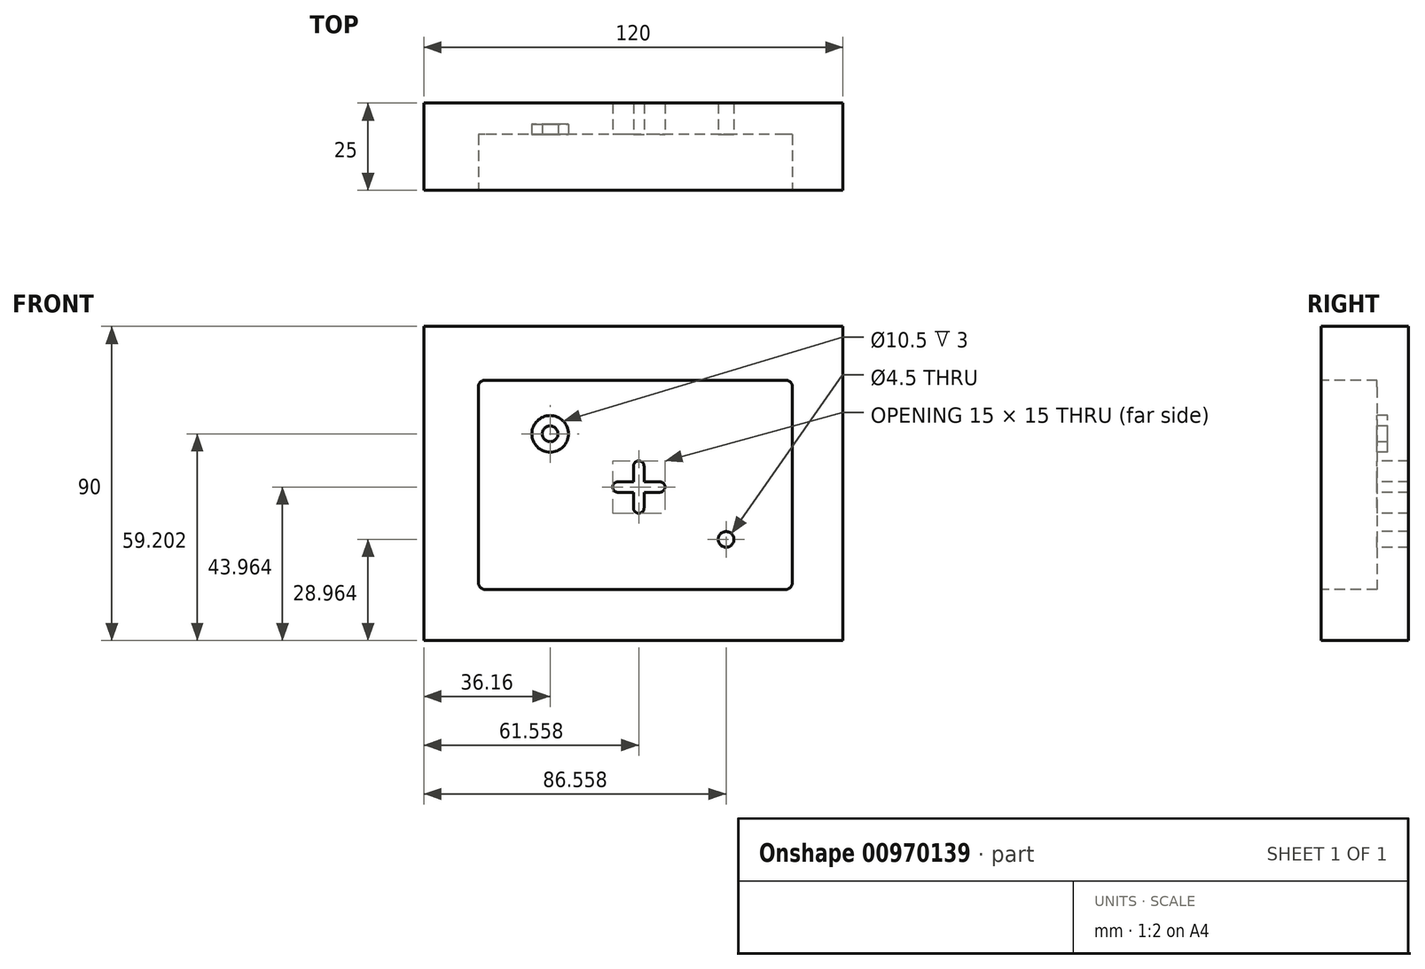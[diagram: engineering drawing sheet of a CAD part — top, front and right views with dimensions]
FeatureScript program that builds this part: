
annotation { "Feature Type Name" : "Feature", "Feature Type Description" : "" }
export const myFeature = defineFeature(function(context is Context, id is Id, definition is map)
    precondition{}
    {
        {
            var Q0;
            Q0=qCreatedBy(makeId("Front.planeOp"),FACE);
            var sketch = newSketch(context, id + "F0", { "sketchPlane" : qUnion([Q0])});
            skLineSegment(sketch, "E0.bottom", {"start": v(60, 45) * mm, "end": v(-60, 45) * mm});
            skLineSegment(sketch, "E0.top", {"start": v(60, -45) * mm, "end": v(-60, -45) * mm});
            skLineSegment(sketch, "E0.left", {"start": v(60, 45) * mm, "end": v(60, -45) * mm});
            skLineSegment(sketch, "E0.right", {"start": v(-60, 45) * mm, "end": v(-60, -45) * mm});
            skPoint(sketch, "E0.middle", {"position": v(0, 0) * mm});
            skLineSegment(sketch, "E1.bottom", {"start": v(43, 30) * mm, "end": v(-43, 30) * mm});
            skLineSegment(sketch, "E1.top", {"start": v(43, -30) * mm, "end": v(-43, -30) * mm});
            skLineSegment(sketch, "E1.left", {"start": v(45, 28) * mm, "end": v(45, -28) * mm});
            skLineSegment(sketch, "E1.right", {"start": v(-45, 28) * mm, "end": v(-45, -28) * mm});
            skPoint(sketch, "E2.visualSharp", {"position": v(-45, 30) * mm});
            skArc(sketch, "E2.filletArc", {"start": v(-43, 30) * mm, "mid": v(-44.41, 29.41) * mm, "end": v(-45, 28) * mm});
            skPoint(sketch, "E3.visualSharp", {"position": v(45, 30) * mm});
            skArc(sketch, "E3.filletArc", {"start": v(45, 28) * mm, "mid": v(44.41, 29.41) * mm, "end": v(43, 30) * mm});
            skPoint(sketch, "E4.visualSharp", {"position": v(45, -30) * mm});
            skArc(sketch, "E4.filletArc", {"start": v(43, -30) * mm, "mid": v(44.41, -29.41) * mm, "end": v(45, -28) * mm});
            skPoint(sketch, "E5.visualSharp", {"position": v(-45, -30) * mm});
            skArc(sketch, "E5.filletArc", {"start": v(-45, -28) * mm, "mid": v(-44.41, -29.41) * mm, "end": v(-43, -30) * mm});
            skCircle(sketch, "E6", {"center": v(-25, 15) * mm, "radius": 2.25 * mm});
            skCircle(sketch, "E7", {"center": v(-25, 15) * mm, "radius": 5.25 * mm});
            skCircle(sketch, "E8", {"center": v(25, -15) * mm, "radius": 2.25 * mm});
            skLineSegment(sketch, "E9.bottom", {"start": v(6, 1.5) * mm, "end": v(1.5, 1.5) * mm});
            skLineSegment(sketch, "E9.top", {"start": v(6, -1.5) * mm, "end": v(1.5, -1.5) * mm});
            skLineSegment(sketch, "E9.left", {"start": v(7.5, 0) * mm, "end": v(7.5, 0) * mm});
            skLineSegment(sketch, "E9.right", {"start": v(-7.5, 0) * mm, "end": v(-7.5, 0) * mm});
            skPoint(sketch, "E10.visualSharp", {"position": v(7.5, 1.5) * mm});
            skArc(sketch, "E10.filletArc", {"start": v(7.5, 0) * mm, "mid": v(7.06, 1.06) * mm, "end": v(6, 1.5) * mm});
            skPoint(sketch, "E11.visualSharp", {"position": v(7.5, -1.5) * mm});
            skArc(sketch, "E11.filletArc", {"start": v(6, -1.5) * mm, "mid": v(7.06, -1.06) * mm, "end": v(7.5, 0) * mm});
            skPoint(sketch, "E12.visualSharp", {"position": v(-7.5, -1.5) * mm});
            skArc(sketch, "E12.filletArc", {"start": v(-7.5, 0) * mm, "mid": v(-7.06, -1.06) * mm, "end": v(-6, -1.5) * mm});
            skPoint(sketch, "E13.visualSharp", {"position": v(-7.5, 1.5) * mm});
            skArc(sketch, "E13.filletArc", {"start": v(-6, 1.5) * mm, "mid": v(-7.06, 1.06) * mm, "end": v(-7.5, 0) * mm});
            skLineSegment(sketch, "E14.1.0", {"start": v(1.5, -6) * mm, "end": v(1.5, -1.5) * mm});
            skArc(sketch, "E14.1.1", {"start": v(1.5, 6) * mm, "mid": v(1.06, 7.06) * mm, "end": v(0, 7.5) * mm});
            skArc(sketch, "E14.1.2", {"start": v(0, 7.5) * mm, "mid": v(-1.06, 7.06) * mm, "end": v(-1.5, 6) * mm});
            skLineSegment(sketch, "E14.1.3", {"start": v(-1.5, -6) * mm, "end": v(-1.5, -1.5) * mm});
            skArc(sketch, "E14.1.4", {"start": v(-1.5, -6) * mm, "mid": v(-1.06, -7.06) * mm, "end": v(0, -7.5) * mm});
            skArc(sketch, "E14.1.5", {"start": v(0, -7.5) * mm, "mid": v(1.06, -7.06) * mm, "end": v(1.5, -6) * mm});
            skLineSegment(sketch, "E14.anchor1", {"start": v(0, 0) * mm, "end": v(-6, 1.5) * mm, "construction": true});
            skLineSegment(sketch, "E14.anchor2", {"start": v(0, 0) * mm, "end": v(1.5, 6) * mm, "construction": true});
            skLineSegment(sketch, "E15.trimOffspring", {"start": v(-1.5, 1.5) * mm, "end": v(-6, 1.5) * mm});
            skLineSegment(sketch, "E16.trimOffspring", {"start": v(-1.5, 1.5) * mm, "end": v(-1.5, 6) * mm});
            skLineSegment(sketch, "E17.trimOffspring", {"start": v(1.5, 1.5) * mm, "end": v(1.5, 6) * mm});
            skLineSegment(sketch, "E18.trimOffspring", {"start": v(-1.5, -1.5) * mm, "end": v(-6, -1.5) * mm});
            skSolve(sketch);
        }
        {
            var Q0;
            Q0=makeQuery(id+"F0.imprint","IMPRINT",FACE,{"disambiguationData":[TD([[makeQuery(id+"F0.imprint","IMPRINT",EDGE,{"derivedFrom":sQuery(id+"F0.wireOp",EDGE,"E1.bottom")}),1.0]])]});
            var Q1;
            Q1=makeQuery(id+"F0.imprint","IMPRINT",FACE,{"disambiguationData":[TD([[makeQuery(id+"F0.imprint","IMPRINT",EDGE,{"derivedFrom":sQuery(id+"F0.wireOp",EDGE,"E0.bottom")}),1.0]])]});
            var Q2;
            Q2=makeQuery(id+"F0.imprint","IMPRINT",FACE,{"disambiguationData":[TD([[makeQuery(id+"F0.imprint","IMPRINT",EDGE,{"derivedFrom":sQuery(id+"F0.wireOp",EDGE,"E6")}),1.0]])]});
            var Q3;
            Q3=makeQuery(id+"F0.imprint","IMPRINT",FACE,{"disambiguationData":[TD([[makeQuery(id+"F0.imprint","IMPRINT",EDGE,{"derivedFrom":sQuery(id+"F0.wireOp",EDGE,"E6")}),-1.0]])]});
            var Q4;
            Q4=makeQuery(id+"F0.imprint","IMPRINT",FACE,{"disambiguationData":[TD([[makeQuery(id+"F0.imprint","IMPRINT",EDGE,{"derivedFrom":sQuery(id+"F0.wireOp",EDGE,"E9.bottom")}),1.0]])]});
            var Q5;
            Q5=makeQuery(id+"F0.imprint","IMPRINT",FACE,{"disambiguationData":[TD([[makeQuery(id+"F0.imprint","IMPRINT",EDGE,{"derivedFrom":sQuery(id+"F0.wireOp",EDGE,"E8")}),1.0]])]});
            extrude(context, id + "F1", {"entities" : qUnion([Q0, Q1, Q2, Q3, Q4, Q5]), "oppositeDirection" : true, "depth" : 25 * mm, "offsetDistance" : 25 * mm});
        }
        {
            var Q0;
            Q0=makeQuery(id+"F1.opExtrude","CAP_FACE",FACE,{"disambiguationData":[OSD([sQuery(id+"F0.wireOp",EDGE,"E0.bottom"),sQuery(id+"F0.wireOp",EDGE,"E0.top"),sQuery(id+"F0.wireOp",EDGE,"E0.left"),sQuery(id+"F0.wireOp",EDGE,"E0.right")])],"isStart":true});
            var sketch = newSketch(context, id + "F2", { "sketchPlane" : qUnion([Q0])});
            skLineSegment(sketch, "E19.bottom", {"start": v(60.58, 44.6) * mm, "end": v(-59.42, 44.6) * mm});
            skLineSegment(sketch, "E19.top", {"start": v(60.58, -45.4) * mm, "end": v(-59.42, -45.4) * mm});
            skLineSegment(sketch, "E19.left", {"start": v(60.58, 44.6) * mm, "end": v(60.58, -45.4) * mm});
            skLineSegment(sketch, "E19.right", {"start": v(-59.42, 44.6) * mm, "end": v(-59.42, -45.4) * mm});
            skPoint(sketch, "E19.middle", {"position": v(0.58, -0.4) * mm});
            skLineSegment(sketch, "E20.bottom", {"start": v(43.58, 29.6) * mm, "end": v(-42.42, 29.6) * mm});
            skLineSegment(sketch, "E20.top", {"start": v(43.58, -30.4) * mm, "end": v(-42.42, -30.4) * mm});
            skLineSegment(sketch, "E20.left", {"start": v(45.58, 27.6) * mm, "end": v(45.58, -28.4) * mm});
            skLineSegment(sketch, "E20.right", {"start": v(-44.42, 27.6) * mm, "end": v(-44.42, -28.4) * mm});
            skPoint(sketch, "E21.visualSharp", {"position": v(-44.42, 29.6) * mm});
            skArc(sketch, "E21.filletArc", {"start": v(-42.42, 29.6) * mm, "mid": v(-43.83, 29.02) * mm, "end": v(-44.42, 27.6) * mm});
            skPoint(sketch, "E22.visualSharp", {"position": v(45.58, 29.6) * mm});
            skArc(sketch, "E22.filletArc", {"start": v(45.58, 27.6) * mm, "mid": v(45, 29.02) * mm, "end": v(43.58, 29.6) * mm});
            skPoint(sketch, "E23.visualSharp", {"position": v(45.58, -30.4) * mm});
            skArc(sketch, "E23.filletArc", {"start": v(43.58, -30.4) * mm, "mid": v(45, -29.81) * mm, "end": v(45.58, -28.4) * mm});
            skPoint(sketch, "E24.visualSharp", {"position": v(-44.42, -30.4) * mm});
            skArc(sketch, "E24.filletArc", {"start": v(-44.42, -28.4) * mm, "mid": v(-43.83, -29.81) * mm, "end": v(-42.42, -30.4) * mm});
            skCircle(sketch, "E25", {"center": v(-24.42, 14.6) * mm, "radius": 2.25 * mm});
            skCircle(sketch, "E26", {"center": v(-24.42, 14.6) * mm, "radius": 5.25 * mm});
            skCircle(sketch, "E27", {"center": v(25.58, -15.4) * mm, "radius": 2.25 * mm});
            skLineSegment(sketch, "E28.bottom", {"start": v(6.58, 1.1) * mm, "end": v(2.08, 1.1) * mm});
            skLineSegment(sketch, "E28.top", {"start": v(6.58, -1.9) * mm, "end": v(2.08, -1.9) * mm});
            skLineSegment(sketch, "E28.left", {"start": v(8.08, -0.4) * mm, "end": v(8.08, -0.4) * mm});
            skLineSegment(sketch, "E28.right", {"start": v(-6.92, -0.4) * mm, "end": v(-6.92, -0.4) * mm});
            skPoint(sketch, "E29.visualSharp", {"position": v(8.08, 1.1) * mm});
            skArc(sketch, "E29.filletArc", {"start": v(8.08, -0.4) * mm, "mid": v(7.64, 0.66) * mm, "end": v(6.58, 1.1) * mm});
            skPoint(sketch, "E30.visualSharp", {"position": v(8.08, -1.9) * mm});
            skArc(sketch, "E30.filletArc", {"start": v(6.58, -1.9) * mm, "mid": v(7.64, -1.46) * mm, "end": v(8.08, -0.4) * mm});
            skPoint(sketch, "E31.visualSharp", {"position": v(-6.92, -1.9) * mm});
            skArc(sketch, "E31.filletArc", {"start": v(-6.92, -0.4) * mm, "mid": v(-6.48, -1.46) * mm, "end": v(-5.42, -1.9) * mm});
            skPoint(sketch, "E32.visualSharp", {"position": v(-6.92, 1.1) * mm});
            skArc(sketch, "E32.filletArc", {"start": v(-5.42, 1.1) * mm, "mid": v(-6.48, 0.66) * mm, "end": v(-6.92, -0.4) * mm});
            skLineSegment(sketch, "E33.1.0", {"start": v(2.08, -6.4) * mm, "end": v(2.08, -1.9) * mm});
            skArc(sketch, "E33.1.1", {"start": v(2.08, 5.6) * mm, "mid": v(1.64, 6.66) * mm, "end": v(0.58, 7.1) * mm});
            skArc(sketch, "E33.1.2", {"start": v(0.58, 7.1) * mm, "mid": v(-0.48, 6.66) * mm, "end": v(-0.92, 5.6) * mm});
            skLineSegment(sketch, "E33.1.3", {"start": v(-0.92, -6.4) * mm, "end": v(-0.92, -1.9) * mm});
            skArc(sketch, "E33.1.4", {"start": v(-0.92, -6.4) * mm, "mid": v(-0.48, -7.46) * mm, "end": v(0.58, -7.9) * mm});
            skArc(sketch, "E33.1.5", {"start": v(0.58, -7.9) * mm, "mid": v(1.64, -7.46) * mm, "end": v(2.08, -6.4) * mm});
            skLineSegment(sketch, "E33.anchor1", {"start": v(0.58, -0.4) * mm, "end": v(-5.42, 1.1) * mm, "construction": true});
            skLineSegment(sketch, "E33.anchor2", {"start": v(0.58, -0.4) * mm, "end": v(2.08, 5.6) * mm, "construction": true});
            skLineSegment(sketch, "E34.trimOffspring", {"start": v(-0.92, 1.1) * mm, "end": v(-5.42, 1.1) * mm});
            skLineSegment(sketch, "E35.trimOffspring", {"start": v(-0.92, 1.1) * mm, "end": v(-0.92, 5.6) * mm});
            skLineSegment(sketch, "E36.trimOffspring", {"start": v(2.08, 1.1) * mm, "end": v(2.08, 5.6) * mm});
            skLineSegment(sketch, "E37.trimOffspring", {"start": v(-0.92, -1.9) * mm, "end": v(-5.42, -1.9) * mm});
            skSolve(sketch);
        }
        {
            var Q0;
            Q0=makeQuery(id+"F2.imprint","IMPRINT",FACE,{"disambiguationData":[TD([[makeQuery(id+"F2.imprint","IMPRINT",EDGE,{"derivedFrom":sQuery(id+"F2.wireOp",EDGE,"E20.bottom")}),1.0]])]});
            var Q1;
            Q1=makeQuery(id+"F2.imprint","IMPRINT",FACE,{"disambiguationData":[TD([[makeQuery(id+"F2.imprint","IMPRINT",EDGE,{"derivedFrom":sQuery(id+"F2.wireOp",EDGE,"E25")}),-1.0]])]});
            var Q2;
            Q2=makeQuery(id+"F2.imprint","IMPRINT",FACE,{"disambiguationData":[TD([[makeQuery(id+"F2.imprint","IMPRINT",EDGE,{"derivedFrom":sQuery(id+"F2.wireOp",EDGE,"E25")}),1.0]])]});
            var Q3;
            Q3=makeQuery(id+"F2.imprint","IMPRINT",FACE,{"disambiguationData":[TD([[makeQuery(id+"F2.imprint","IMPRINT",EDGE,{"derivedFrom":sQuery(id+"F2.wireOp",EDGE,"E28.bottom")}),1.0]])]});
            var Q4;
            Q4=makeQuery(id+"F2.imprint","IMPRINT",FACE,{"disambiguationData":[TD([[makeQuery(id+"F2.imprint","IMPRINT",EDGE,{"derivedFrom":sQuery(id+"F2.wireOp",EDGE,"E27")}),1.0]])]});
            extrude(context, id + "F3", {"entities" : qUnion([Q0, Q1, Q2, Q3, Q4]), "operationType" : NewBodyOperationType.REMOVE, "oppositeDirection" : true, "depth" : 16 * mm, "offsetDistance" : 25 * mm});
        }
        {
            var Q0;
            Q0=makeQuery(id+"F3.boolean.opBoolean","COPY",FACE,{"derivedFrom":makeQuery(id+"F3.opExtrude","CAP_FACE",FACE,{"disambiguationData":[OSD([sQuery(id+"F2.wireOp",EDGE,"E20.bottom"),sQuery(id+"F2.wireOp",EDGE,"E20.top"),sQuery(id+"F2.wireOp",EDGE,"E20.left"),sQuery(id+"F2.wireOp",EDGE,"E20.right"),sQuery(id+"F2.wireOp",EDGE,"E21.filletArc"),sQuery(id+"F2.wireOp",EDGE,"E22.filletArc"),sQuery(id+"F2.wireOp",EDGE,"E23.filletArc"),sQuery(id+"F2.wireOp",EDGE,"E24.filletArc")])],"isStart":false})});
            var sketch = newSketch(context, id + "F4", { "sketchPlane" : qUnion([Q0])});
            skLineSegment(sketch, "E38.bottom", {"start": v(61.16, 44.2) * mm, "end": v(-58.84, 44.2) * mm});
            skLineSegment(sketch, "E38.top", {"start": v(61.16, -45.8) * mm, "end": v(-58.84, -45.8) * mm});
            skLineSegment(sketch, "E38.left", {"start": v(61.16, 44.2) * mm, "end": v(61.16, -45.8) * mm});
            skLineSegment(sketch, "E38.right", {"start": v(-58.84, 44.2) * mm, "end": v(-58.84, -45.8) * mm});
            skPoint(sketch, "E38.middle", {"position": v(1.16, -0.8) * mm});
            skLineSegment(sketch, "E39.bottom", {"start": v(44.16, 29.2) * mm, "end": v(-41.84, 29.2) * mm});
            skLineSegment(sketch, "E39.top", {"start": v(44.16, -30.8) * mm, "end": v(-41.84, -30.8) * mm});
            skLineSegment(sketch, "E39.left", {"start": v(46.16, 27.2) * mm, "end": v(46.16, -28.8) * mm});
            skLineSegment(sketch, "E39.right", {"start": v(-43.84, 27.2) * mm, "end": v(-43.84, -28.8) * mm});
            skPoint(sketch, "E40.visualSharp", {"position": v(-43.84, 29.2) * mm});
            skArc(sketch, "E40.filletArc", {"start": v(-41.84, 29.2) * mm, "mid": v(-43.25, 28.62) * mm, "end": v(-43.84, 27.2) * mm});
            skPoint(sketch, "E41.visualSharp", {"position": v(46.16, 29.2) * mm});
            skArc(sketch, "E41.filletArc", {"start": v(46.16, 27.2) * mm, "mid": v(45.57, 28.62) * mm, "end": v(44.16, 29.2) * mm});
            skPoint(sketch, "E42.visualSharp", {"position": v(46.16, -30.8) * mm});
            skArc(sketch, "E42.filletArc", {"start": v(44.16, -30.8) * mm, "mid": v(45.57, -30.21) * mm, "end": v(46.16, -28.8) * mm});
            skPoint(sketch, "E43.visualSharp", {"position": v(-43.84, -30.8) * mm});
            skArc(sketch, "E43.filletArc", {"start": v(-43.84, -28.8) * mm, "mid": v(-43.25, -30.21) * mm, "end": v(-41.84, -30.8) * mm});
            skCircle(sketch, "E44", {"center": v(-23.84, 14.2) * mm, "radius": 2.25 * mm});
            skCircle(sketch, "E45", {"center": v(-23.84, 14.2) * mm, "radius": 5.25 * mm});
            skCircle(sketch, "E46", {"center": v(26.16, -15.8) * mm, "radius": 2.25 * mm});
            skLineSegment(sketch, "E47.bottom", {"start": v(7.16, 0.7) * mm, "end": v(2.66, 0.7) * mm});
            skLineSegment(sketch, "E47.top", {"start": v(7.16, -2.3) * mm, "end": v(2.66, -2.3) * mm});
            skLineSegment(sketch, "E47.left", {"start": v(8.66, -0.8) * mm, "end": v(8.66, -0.8) * mm});
            skLineSegment(sketch, "E47.right", {"start": v(-6.34, -0.8) * mm, "end": v(-6.34, -0.8) * mm});
            skPoint(sketch, "E48.visualSharp", {"position": v(8.66, 0.7) * mm});
            skArc(sketch, "E48.filletArc", {"start": v(8.66, -0.8) * mm, "mid": v(8.22, 0.26) * mm, "end": v(7.16, 0.7) * mm});
            skPoint(sketch, "E49.visualSharp", {"position": v(8.66, -2.3) * mm});
            skArc(sketch, "E49.filletArc", {"start": v(7.16, -2.3) * mm, "mid": v(8.22, -1.86) * mm, "end": v(8.66, -0.8) * mm});
            skPoint(sketch, "E50.visualSharp", {"position": v(-6.34, -2.3) * mm});
            skArc(sketch, "E50.filletArc", {"start": v(-6.34, -0.8) * mm, "mid": v(-5.9, -1.86) * mm, "end": v(-4.84, -2.3) * mm});
            skPoint(sketch, "E51.visualSharp", {"position": v(-6.34, 0.7) * mm});
            skArc(sketch, "E51.filletArc", {"start": v(-4.84, 0.7) * mm, "mid": v(-5.9, 0.26) * mm, "end": v(-6.34, -0.8) * mm});
            skLineSegment(sketch, "E52.1.0", {"start": v(2.66, -6.8) * mm, "end": v(2.66, -2.3) * mm});
            skArc(sketch, "E52.1.1", {"start": v(2.66, 5.2) * mm, "mid": v(2.22, 6.26) * mm, "end": v(1.16, 6.7) * mm});
            skArc(sketch, "E52.1.2", {"start": v(1.16, 6.7) * mm, "mid": v(0.1, 6.26) * mm, "end": v(-0.34, 5.2) * mm});
            skLineSegment(sketch, "E52.1.3", {"start": v(-0.34, -6.8) * mm, "end": v(-0.34, -2.3) * mm});
            skArc(sketch, "E52.1.4", {"start": v(-0.34, -6.8) * mm, "mid": v(0.1, -7.86) * mm, "end": v(1.16, -8.3) * mm});
            skArc(sketch, "E52.1.5", {"start": v(1.16, -8.3) * mm, "mid": v(2.22, -7.86) * mm, "end": v(2.66, -6.8) * mm});
            skLineSegment(sketch, "E52.anchor1", {"start": v(1.16, -0.8) * mm, "end": v(-4.84, 0.7) * mm, "construction": true});
            skLineSegment(sketch, "E52.anchor2", {"start": v(1.16, -0.8) * mm, "end": v(2.66, 5.2) * mm, "construction": true});
            skLineSegment(sketch, "E53.trimOffspring", {"start": v(-0.34, 0.7) * mm, "end": v(-4.84, 0.7) * mm});
            skLineSegment(sketch, "E54.trimOffspring", {"start": v(-0.34, 0.7) * mm, "end": v(-0.34, 5.2) * mm});
            skLineSegment(sketch, "E55.trimOffspring", {"start": v(2.66, 0.7) * mm, "end": v(2.66, 5.2) * mm});
            skLineSegment(sketch, "E56.trimOffspring", {"start": v(-0.34, -2.3) * mm, "end": v(-4.84, -2.3) * mm});
            skSolve(sketch);
        }
        {
            var Q0;
            Q0=makeQuery(id+"F4.imprint","IMPRINT",FACE,{"disambiguationData":[TD([[makeQuery(id+"F4.imprint","IMPRINT",EDGE,{"derivedFrom":sQuery(id+"F4.wireOp",EDGE,"E44")}),-1.0]])]});
            extrude(context, id + "F5", {"entities" : qUnion([Q0]), "operationType" : NewBodyOperationType.REMOVE, "oppositeDirection" : true, "depth" : 3 * mm, "offsetDistance" : 25 * mm});
        }
        {
            var Q0;
            {var subQ0=sQuery(id+"F2.wireOp",EDGE,"E20.right");var subQ1=sQuery(id+"F2.wireOp",EDGE,"E20.left");var subQ2=sQuery(id+"F2.wireOp",EDGE,"E20.top");var subQ3=sQuery(id+"F2.wireOp",EDGE,"E20.bottom");var subQ4=sQuery(id+"F2.wireOp",EDGE,"E21.filletArc");var subQ5=sQuery(id+"F2.wireOp",EDGE,"E22.filletArc");var subQ6=sQuery(id+"F2.wireOp",EDGE,"E23.filletArc");var subQ7=sQuery(id+"F2.wireOp",EDGE,"E24.filletArc");Q0=makeQuery(id+"F5.boolean.opBoolean","SPLIT",FACE,{"disambiguationData":[TD([makeQuery(id+"F3.boolean.opBoolean","COPY",FACE,{"derivedFrom":makeQuery(id+"F3.opExtrude","SWEPT_FACE",FACE,{"disambiguationData":[OSD([subQ3])]})})])],"derivedFrom":makeQuery(id+"F3.boolean.opBoolean","COPY",FACE,{"derivedFrom":makeQuery(id+"F3.opExtrude","CAP_FACE",FACE,{"disambiguationData":[OSD([subQ3,subQ2,subQ1,subQ0,subQ4,subQ5,subQ6,subQ7])],"isStart":false})})});}
            var sketch = newSketch(context, id + "F6", { "sketchPlane" : qUnion([Q0])});
            skLineSegment(sketch, "E57.bottom", {"start": v(61.56, 43.96) * mm, "end": v(-58.44, 43.96) * mm});
            skLineSegment(sketch, "E57.top", {"start": v(61.56, -46.04) * mm, "end": v(-58.44, -46.04) * mm});
            skLineSegment(sketch, "E57.left", {"start": v(61.56, 43.96) * mm, "end": v(61.56, -46.04) * mm});
            skLineSegment(sketch, "E57.right", {"start": v(-58.44, 43.96) * mm, "end": v(-58.44, -46.04) * mm});
            skPoint(sketch, "E57.middle", {"position": v(1.56, -1.04) * mm});
            skLineSegment(sketch, "E58.bottom", {"start": v(44.56, 28.96) * mm, "end": v(-41.44, 28.96) * mm});
            skLineSegment(sketch, "E58.top", {"start": v(44.56, -31.04) * mm, "end": v(-41.44, -31.04) * mm});
            skLineSegment(sketch, "E58.left", {"start": v(46.56, 26.96) * mm, "end": v(46.56, -29.04) * mm});
            skLineSegment(sketch, "E58.right", {"start": v(-43.44, 26.96) * mm, "end": v(-43.44, -29.04) * mm});
            skPoint(sketch, "E59.visualSharp", {"position": v(-43.44, 28.96) * mm});
            skArc(sketch, "E59.filletArc", {"start": v(-41.44, 28.96) * mm, "mid": v(-42.86, 28.38) * mm, "end": v(-43.44, 26.96) * mm});
            skPoint(sketch, "E60.visualSharp", {"position": v(46.56, 28.96) * mm});
            skArc(sketch, "E60.filletArc", {"start": v(46.56, 26.96) * mm, "mid": v(45.97, 28.38) * mm, "end": v(44.56, 28.96) * mm});
            skPoint(sketch, "E61.visualSharp", {"position": v(46.56, -31.04) * mm});
            skArc(sketch, "E61.filletArc", {"start": v(44.56, -31.04) * mm, "mid": v(45.97, -30.45) * mm, "end": v(46.56, -29.04) * mm});
            skPoint(sketch, "E62.visualSharp", {"position": v(-43.44, -31.04) * mm});
            skArc(sketch, "E62.filletArc", {"start": v(-43.44, -29.04) * mm, "mid": v(-42.86, -30.45) * mm, "end": v(-41.44, -31.04) * mm});
            skCircle(sketch, "E63", {"center": v(-23.44, 13.96) * mm, "radius": 2.25 * mm});
            skCircle(sketch, "E64", {"center": v(-23.44, 13.96) * mm, "radius": 5.25 * mm});
            skCircle(sketch, "E65", {"center": v(26.56, -16.04) * mm, "radius": 2.25 * mm});
            skLineSegment(sketch, "E66.bottom", {"start": v(7.56, 0.46) * mm, "end": v(3.06, 0.46) * mm});
            skLineSegment(sketch, "E66.top", {"start": v(7.56, -2.54) * mm, "end": v(3.06, -2.54) * mm});
            skLineSegment(sketch, "E66.left", {"start": v(9.06, -1.04) * mm, "end": v(9.06, -1.04) * mm});
            skLineSegment(sketch, "E66.right", {"start": v(-5.94, -1.04) * mm, "end": v(-5.94, -1.04) * mm});
            skPoint(sketch, "E67.visualSharp", {"position": v(9.06, 0.46) * mm});
            skArc(sketch, "E67.filletArc", {"start": v(9.06, -1.04) * mm, "mid": v(8.62, 0.02) * mm, "end": v(7.56, 0.46) * mm});
            skPoint(sketch, "E68.visualSharp", {"position": v(9.06, -2.54) * mm});
            skArc(sketch, "E68.filletArc", {"start": v(7.56, -2.54) * mm, "mid": v(8.62, -2.1) * mm, "end": v(9.06, -1.04) * mm});
            skPoint(sketch, "E69.visualSharp", {"position": v(-5.94, -2.54) * mm});
            skArc(sketch, "E69.filletArc", {"start": v(-5.94, -1.04) * mm, "mid": v(-5.5, -2.1) * mm, "end": v(-4.44, -2.54) * mm});
            skPoint(sketch, "E70.visualSharp", {"position": v(-5.94, 0.46) * mm});
            skArc(sketch, "E70.filletArc", {"start": v(-4.44, 0.46) * mm, "mid": v(-5.5, 0.02) * mm, "end": v(-5.94, -1.04) * mm});
            skLineSegment(sketch, "E71.1.0", {"start": v(3.06, -7.04) * mm, "end": v(3.06, -2.54) * mm});
            skArc(sketch, "E71.1.1", {"start": v(3.06, 4.96) * mm, "mid": v(2.62, 6.02) * mm, "end": v(1.56, 6.46) * mm});
            skArc(sketch, "E71.1.2", {"start": v(1.56, 6.46) * mm, "mid": v(0.5, 6.02) * mm, "end": v(0.06, 4.96) * mm});
            skLineSegment(sketch, "E71.1.3", {"start": v(0.06, -7.04) * mm, "end": v(0.06, -2.54) * mm});
            skArc(sketch, "E71.1.4", {"start": v(0.06, -7.04) * mm, "mid": v(0.5, -8.1) * mm, "end": v(1.56, -8.54) * mm});
            skArc(sketch, "E71.1.5", {"start": v(1.56, -8.54) * mm, "mid": v(2.62, -8.1) * mm, "end": v(3.06, -7.04) * mm});
            skLineSegment(sketch, "E71.anchor1", {"start": v(1.56, -1.04) * mm, "end": v(-4.44, 0.46) * mm, "construction": true});
            skLineSegment(sketch, "E71.anchor2", {"start": v(1.56, -1.04) * mm, "end": v(3.06, 4.96) * mm, "construction": true});
            skLineSegment(sketch, "E72.trimOffspring", {"start": v(0.06, 0.46) * mm, "end": v(-4.44, 0.46) * mm});
            skLineSegment(sketch, "E73.trimOffspring", {"start": v(0.06, 0.46) * mm, "end": v(0.06, 4.96) * mm});
            skLineSegment(sketch, "E74.trimOffspring", {"start": v(3.06, 0.46) * mm, "end": v(3.06, 4.96) * mm});
            skLineSegment(sketch, "E75.trimOffspring", {"start": v(0.06, -2.54) * mm, "end": v(-4.44, -2.54) * mm});
            skSolve(sketch);
        }
        {
            var Q0;
            Q0=makeQuery(id+"F6.imprint","IMPRINT",FACE,{"disambiguationData":[TD([[makeQuery(id+"F6.imprint","IMPRINT",EDGE,{"derivedFrom":sQuery(id+"F6.wireOp",EDGE,"E66.bottom")}),1.0]])]});
            var Q1;
            Q1=makeQuery(id+"F6.imprint","IMPRINT",FACE,{"disambiguationData":[TD([[makeQuery(id+"F6.imprint","IMPRINT",EDGE,{"derivedFrom":sQuery(id+"F6.wireOp",EDGE,"E65")}),1.0]])]});
            extrude(context, id + "F7", {"entities" : qUnion([Q0, Q1]), "operationType" : NewBodyOperationType.REMOVE, "endBound" : BoundingType.THROUGH_ALL, "oppositeDirection" : true, "depth" : 25 * mm, "offsetDistance" : 25 * mm});
        }
    });
